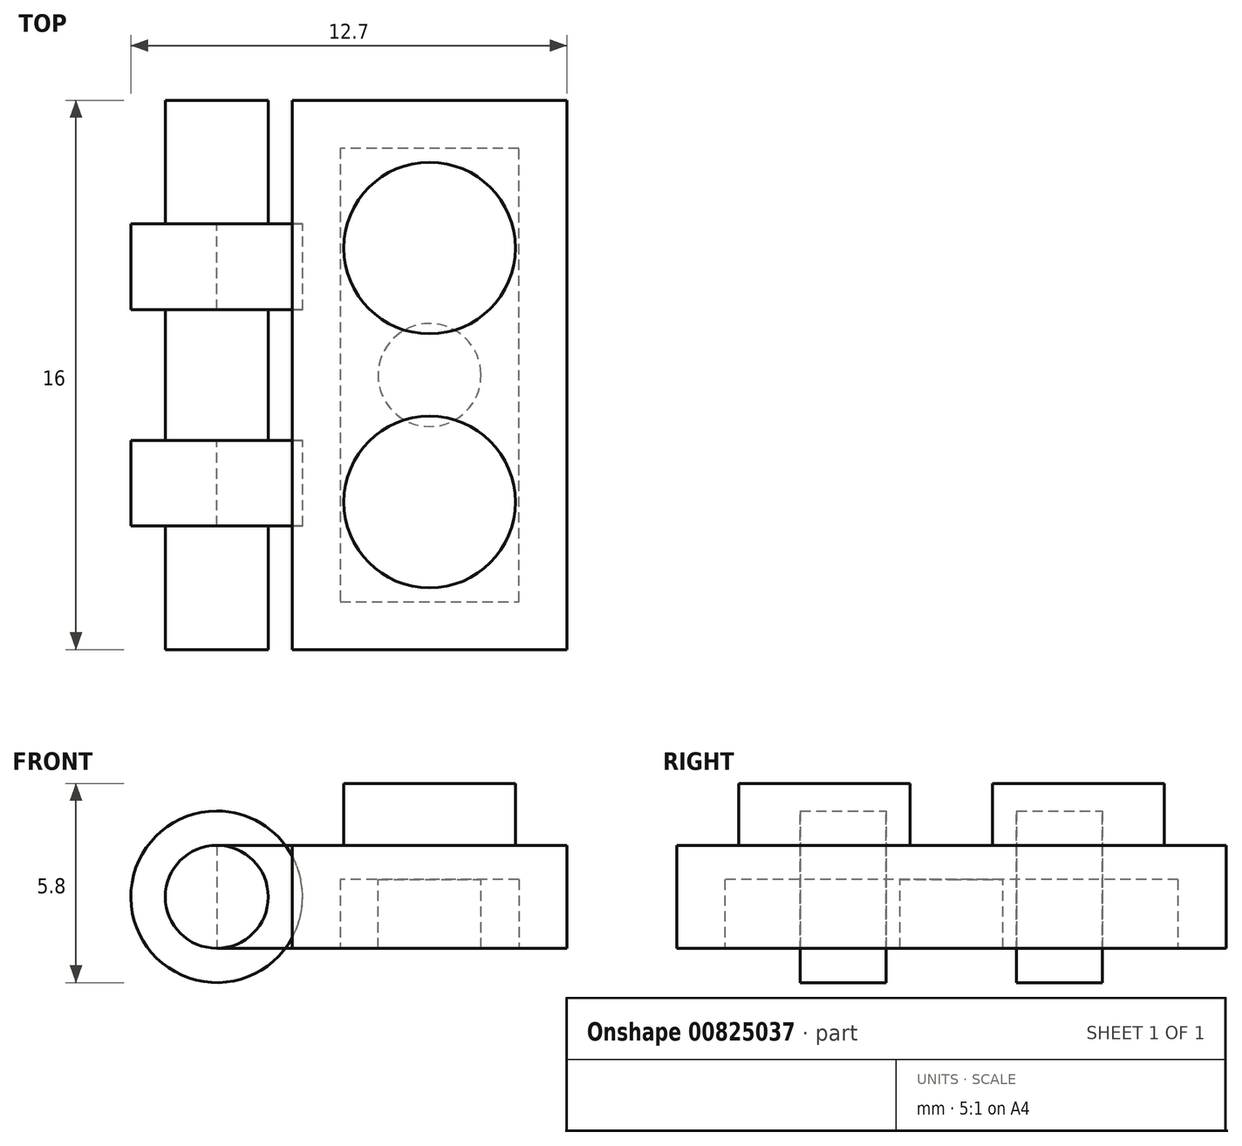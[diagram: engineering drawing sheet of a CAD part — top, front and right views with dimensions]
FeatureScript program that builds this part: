
annotation { "Feature Type Name" : "Feature", "Feature Type Description" : "" }
export const myFeature = defineFeature(function(context is Context, id is Id, definition is map)
    precondition{}
    {
        {
            var Q0;
            Q0=qCreatedBy(makeId("Front.planeOp"),FACE);
            var sketch = newSketch(context, id + "F0", { "sketchPlane" : qUnion([Q0])});
            skLineSegment(sketch, "E0", {"start": v(0, 0) * mm, "end": v(-8, 0) * mm});
            skLineSegment(sketch, "E1", {"start": v(-8, 0) * mm, "end": v(-8, -3) * mm});
            skLineSegment(sketch, "E2", {"start": v(-8, -3) * mm, "end": v(0, -3) * mm});
            skLineSegment(sketch, "E3", {"start": v(0, -3) * mm, "end": v(0, 0) * mm});
            skSolve(sketch);
        }
        {
            var Q0;
            Q0 = qSketchRegion(id + "F0", true);
            extrude(context, id + "F1", {"entities" : qUnion([Q0]), "depth" : 16 * mm, "offsetDistance" : 25 * mm});
        }
        {
            var Q0;
            Q0=makeQuery(id+"F1.opExtrude","SWEPT_FACE",FACE,{"disambiguationData":[OSD([sQuery(id+"F0.wireOp",EDGE,"E0")])]});
            var sketch = newSketch(context, id + "F2", { "sketchPlane" : qUnion([Q0])});
            skCircle(sketch, "E4", {"center": v(-4, -4.3) * mm, "radius": 2.5 * mm});
            skPoint(sketch, "E4.centerSnap0", {"position": v(-4, 0) * mm});
            skCircle(sketch, "E5", {"center": v(-4, -11.7) * mm, "radius": 2.5 * mm});
            skPoint(sketch, "E5.centerSnap0", {"position": v(-4, -16) * mm});
            skSolve(sketch);
        }
        {
            var Q0;
            Q0 = qSketchRegion(id + "F2", true);
            extrude(context, id + "F3", {"entities" : qUnion([Q0]), "operationType" : NewBodyOperationType.ADD, "depth" : 1.8 * mm, "offsetDistance" : 25 * mm});
        }
        {
            var Q0;
            Q0=makeQuery(id+"F1.opExtrude","SWEPT_FACE",FACE,{"disambiguationData":[OSD([sQuery(id+"F0.wireOp",EDGE,"E1")])]});
            var sketch = newSketch(context, id + "F4", { "sketchPlane" : qUnion([Q0])});
            skLineSegment(sketch, "E6", {"start": v(9.9, 0) * mm, "end": v(9.9, -3) * mm});
            skLineSegment(sketch, "E7", {"start": v(12.4, 0) * mm, "end": v(12.4, -3) * mm});
            skLineSegment(sketch, "E8", {"start": v(3.6, 0) * mm, "end": v(3.6, -3) * mm});
            skLineSegment(sketch, "E9", {"start": v(6.1, 0) * mm, "end": v(6.1, -3) * mm});
            skSolve(sketch);
        }
        {
            var Q0;
            Q0 = qSketchRegion(id + "F4", true);
            var Q1;
            {var subQ0=sQuery(id+"F4.wireOp",EDGE,"E8");Q1=makeQuery(id+"F4.imprint","IMPRINT",FACE,{"disambiguationData":[TD([[makeQuery(id+"F4.imprint","IMPRINT",EDGE,{"derivedFrom":subQ0}),1.0]])]});}
            var Q2;
            {var subQ0=sQuery(id+"F4.wireOp",EDGE,"E6");Q2=makeQuery(id+"F4.imprint","IMPRINT",FACE,{"disambiguationData":[TD([[makeQuery(id+"F4.imprint","IMPRINT",EDGE,{"derivedFrom":subQ0}),1.0]])]});}
            extrude(context, id + "F5", {"entities" : qUnion([Q0, Q1, Q2]), "depth" : 2.2 * mm, "offsetDistance" : 25 * mm});
        }
        {
            var Q0;
            Q0=makeQuery(id+"F5.opExtrude","CAP_FACE",FACE,{"disambiguationData":[OSD([sQuery(id+"F0.wireOp",EDGE,"E0"),sQuery(id+"F0.wireOp",EDGE,"E1"),sQuery(id+"F0.wireOp",EDGE,"E2"),sQuery(id+"F4.wireOp",EDGE,"E6"),sQuery(id+"F4.wireOp",EDGE,"E7")])],"isStart":false});
            var sketch = newSketch(context, id + "F6", { "sketchPlane" : qUnion([Q0])});
            skLineSegment(sketch, "E10", {"start": v(9.9, -3) * mm, "end": v(0, -3) * mm});
            skLineSegment(sketch, "E11", {"start": v(0, -3) * mm, "end": v(0, -1.5) * mm});
            skLineSegment(sketch, "E12", {"start": v(16, -1.5) * mm, "end": v(16, -3) * mm});
            skLineSegment(sketch, "E13", {"start": v(16, -3) * mm, "end": v(9.9, -3) * mm});
            skLineSegment(sketch, "E14", {"start": v(0, -1.5) * mm, "end": v(16, -1.5) * mm});
            skLineSegment(sketch, "E15", {"start": v(9.9, -3) * mm, "end": v(9.9, -4) * mm});
            skLineSegment(sketch, "E16", {"start": v(9.9, -4) * mm, "end": v(12.4, -4) * mm});
            skLineSegment(sketch, "E17", {"start": v(12.4, -4) * mm, "end": v(12.4, -3) * mm});
            skLineSegment(sketch, "E18", {"start": v(6.1, -3) * mm, "end": v(6.1, -4) * mm});
            skLineSegment(sketch, "E19", {"start": v(6.1, -4) * mm, "end": v(3.6, -4) * mm});
            skLineSegment(sketch, "E20", {"start": v(3.6, -4) * mm, "end": v(3.6, -3) * mm});
            skPoint(sketch, "E21.orphan", {"position": v(0, 0) * mm});
            skPoint(sketch, "E22.orphan", {"position": v(16, 0) * mm});
            skSolve(sketch);
        }
        {
            var Q0;
            {var subQ0=sQuery(id+"F6.wireOp",EDGE,"E18");Q0=makeQuery(id+"F6.imprint","IMPRINT",FACE,{"disambiguationData":[TD([[makeQuery(id+"F6.imprint","IMPRINT",EDGE,{"derivedFrom":subQ0}),-1.0]])]});}
            var Q1;
            {var subQ0=sQuery(id+"F6.wireOp",EDGE,"E15");Q1=makeQuery(id+"F6.imprint","IMPRINT",FACE,{"disambiguationData":[TD([[makeQuery(id+"F6.imprint","IMPRINT",EDGE,{"derivedFrom":subQ0}),1.0]])]});}
            var Q2;
            {var subQ0=sQuery(id+"F6.wireOp",EDGE,"E12");Q2=makeQuery(id+"F6.imprint","IMPRINT",FACE,{"disambiguationData":[TD([[makeQuery(id+"F6.imprint","IMPRINT",EDGE,{"derivedFrom":subQ0}),-1.0]])]});}
            var Q3;
            {var subQ1=makeQuery(id+"F5.opExtrude","CAP_EDGE",EDGE,{"disambiguationData":[OSD([sQuery(id+"F4.wireOp",EDGE,"E6")])],"isStart":false});var subQ5=sQuery(id+"F6.wireOp",EDGE,"E14");var subQ6=makeQuery(id+"F6.imprint","INTERSECT",VERTEX,{"derivedFrom":[subQ1,subQ5]});Q3=makeQuery(id+"F6.imprint","IMPRINT",FACE,{"disambiguationData":[TD([[makeQuery(id+"F6.imprint","IMPRINT",EDGE,{"disambiguationData":[TD([[subQ6,-1.0]])],"derivedFrom":subQ5}),-1.0]])]});}
            var Q4;
            {var subQ0=sQuery(id+"F6.wireOp",EDGE,"E11");Q4=makeQuery(id+"F6.imprint","IMPRINT",FACE,{"disambiguationData":[TD([[makeQuery(id+"F6.imprint","IMPRINT",EDGE,{"derivedFrom":subQ0}),-1.0]])]});}
            var Q5;
            Q5=sQuery(id+"F6.wireOp",EDGE,"E14");
            revolve(context, id + "F7", {"surfaceOperationType" : NewSurfaceOperationType.NEW, "entities" : qUnion([Q0, Q1, Q2, Q3, Q4]), "axis" : qUnion([Q5]), "revolveType" : RevolveType.FULL});
        }
        {
            var Q0;
            Q0=makeQuery(id+"F1.opExtrude","SWEPT_FACE",FACE,{"disambiguationData":[OSD([sQuery(id+"F0.wireOp",EDGE,"E2")])]});
            var sketch = newSketch(context, id + "F8", { "sketchPlane" : qUnion([Q0])});
            skLineSegment(sketch, "E23", {"start": v(-6.6, 8) * mm, "end": v(-6.6, 14.6) * mm});
            skPoint(sketch, "E23.startSnap0", {"position": v(-8, 8) * mm});
            skLineSegment(sketch, "E24", {"start": v(-6.6, 14.6) * mm, "end": v(-1.4, 14.6) * mm});
            skLineSegment(sketch, "E25", {"start": v(-1.4, 14.6) * mm, "end": v(-1.4, 1.4) * mm});
            skLineSegment(sketch, "E26", {"start": v(-1.4, 1.4) * mm, "end": v(-6.6, 1.4) * mm});
            skLineSegment(sketch, "E27", {"start": v(-6.6, 1.4) * mm, "end": v(-6.6, 8) * mm});
            skSolve(sketch);
        }
        {
            var Q0;
            Q0 = qSketchRegion(id + "F8", true);
            extrude(context, id + "F9", {"entities" : qUnion([Q0]), "operationType" : NewBodyOperationType.REMOVE, "oppositeDirection" : true, "depth" : 2 * mm, "offsetDistance" : 25 * mm});
        }
        {
            var Q0;
            Q0=makeQuery(id+"F9.boolean.opBoolean","COPY",FACE,{"derivedFrom":makeQuery(id+"F9.opExtrude","CAP_FACE",FACE,{"disambiguationData":[OSD([sQuery(id+"F8.wireOp",EDGE,"E23"),sQuery(id+"F8.wireOp",EDGE,"E24"),sQuery(id+"F8.wireOp",EDGE,"E25"),sQuery(id+"F8.wireOp",EDGE,"E26"),sQuery(id+"F8.wireOp",EDGE,"E27")])],"isStart":false})});
            var sketch = newSketch(context, id + "F10", { "sketchPlane" : qUnion([Q0])});
            skCircle(sketch, "E28", {"center": v(-4, 8) * mm, "radius": 1.5 * mm});
            skPoint(sketch, "E28.centerSnap0", {"position": v(-4, 14.6) * mm});
            skPoint(sketch, "E28.centerSnap1", {"position": v(-6.6, 8) * mm});
            skSolve(sketch);
        }
        {
            var Q0;
            Q0 = qSketchRegion(id + "F10", true);
            extrude(context, id + "F11", {"entities" : qUnion([Q0]), "operationType" : NewBodyOperationType.ADD, "depth" : 2 * mm, "offsetDistance" : 25 * mm});
        }
    });
